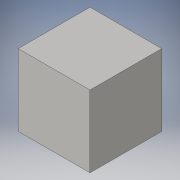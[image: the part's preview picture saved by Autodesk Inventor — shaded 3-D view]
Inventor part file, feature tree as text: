
AUTODESK INVENTOR PART (.ipt)
format: ipt  version: 2016 (Build 200138000, 138)  size: 79,872 bytes
history: native  units: in
note: dims shown in document units (in); Inventor stores cm internally (conversion verified against a paired STEP export)
features: extrude x1, sketch x1
ambient origin geometry x8: Origin, YZ Plane, XZ Plane, XY Plane, X Axis, Y Axis, Z Axis, Center Point
bodies: Solid1 (feature_tree)
feature tree (2):
  extrude  "Extrusion1"  Depth=1.1811in
  sketch  "Sketch1"  dims[d0=1.1811in d1=1.1811in d2=1.1811in d3=0.0in]
